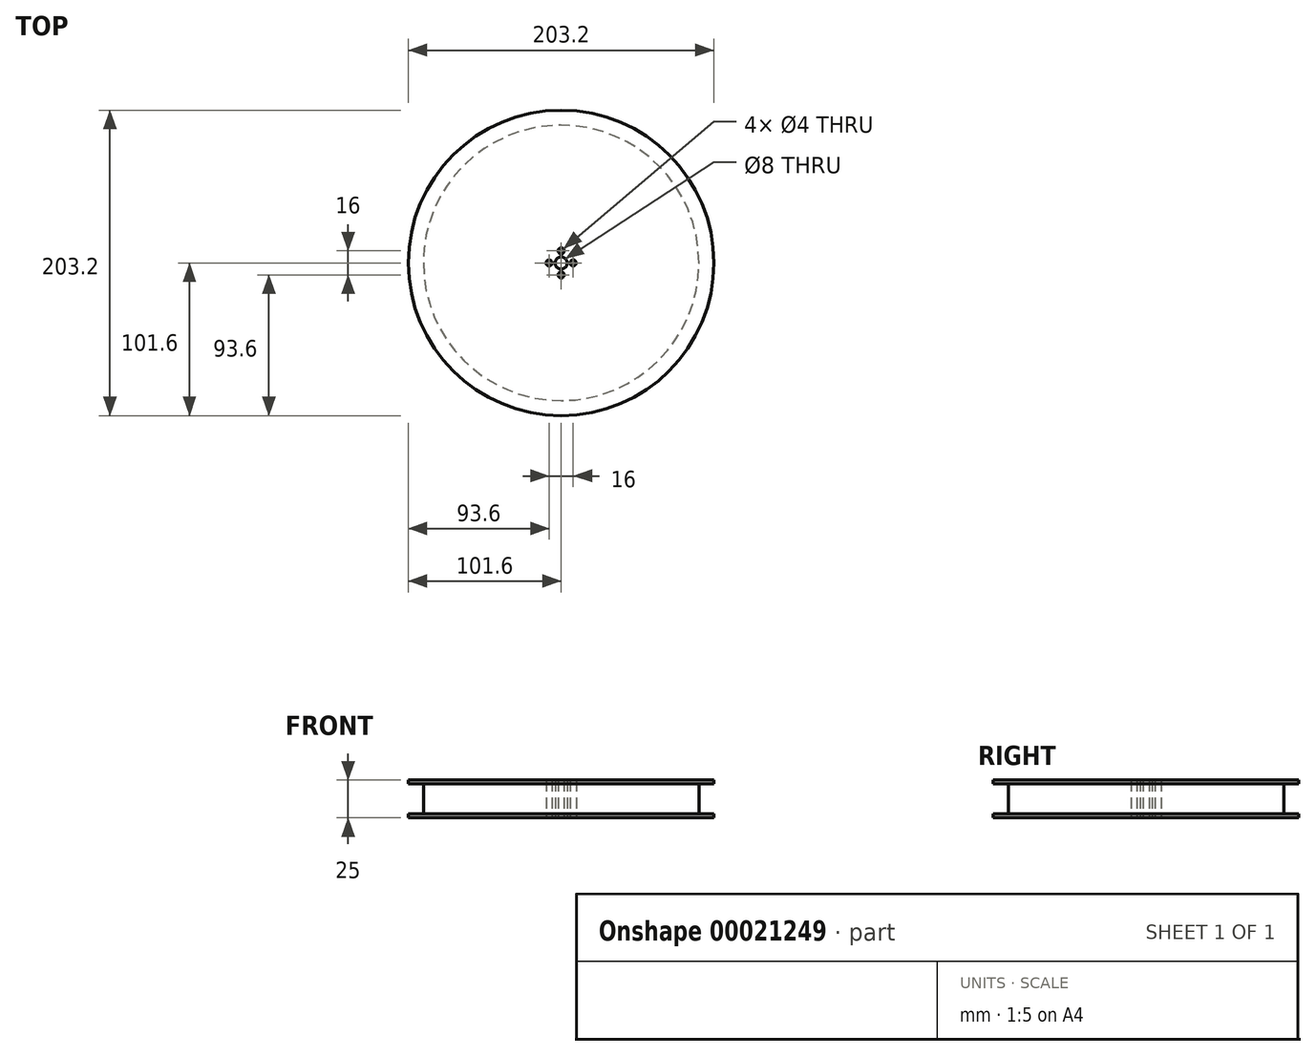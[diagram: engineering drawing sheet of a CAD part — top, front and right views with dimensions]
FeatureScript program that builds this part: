
annotation { "Feature Type Name" : "Feature", "Feature Type Description" : "" }
export const myFeature = defineFeature(function(context is Context, id is Id, definition is map)
    precondition{}
    {
        {
            var Q0;
            Q0=qCreatedBy(makeId("Top.planeOp"),FACE);
            var sketch = newSketch(context, id + "F0", { "sketchPlane" : qUnion([Q0])});
            skCircle(sketch, "E0", {"center": v(0, 0) * mm, "radius": 4 * mm});
            skCircle(sketch, "E1", {"center": v(8, 0) * mm, "radius": 2 * mm});
            skCircle(sketch, "E2.1.0", {"center": v(0, 8) * mm, "radius": 2 * mm});
            skCircle(sketch, "E2.2.0", {"center": v(-8, 0) * mm, "radius": 2 * mm});
            skCircle(sketch, "E2.3.0", {"center": v(0, -8) * mm, "radius": 2 * mm});
            skCircle(sketch, "E3", {"center": v(0, 0) * mm, "radius": 12 * mm});
            skCircle(sketch, "E4", {"center": v(0, 0) * mm, "radius": 101.6 * mm});
            skCircle(sketch, "E5", {"center": v(0, 0) * mm, "radius": 91.6 * mm});
            skSolve(sketch);
        }
        {
            var Q0;
            Q0=makeQuery(id+"F0.imprint","IMPRINT",FACE,{"disambiguationData":[TD([[makeQuery(id+"F0.imprint","IMPRINT",EDGE,{"derivedFrom":sQuery(id+"F0.wireOp",EDGE,"E0")}),-1.0]])]});
            var Q1;
            Q1=makeQuery(id+"F0.imprint","IMPRINT",FACE,{"disambiguationData":[TD([[makeQuery(id+"F0.imprint","IMPRINT",EDGE,{"derivedFrom":sQuery(id+"F0.wireOp",EDGE,"E3")}),-1.0]])]});
            extrude(context, id + "F1", {"entities" : qUnion([Q0, Q1]), "endBound" : BoundingType.SYMMETRIC, "depth" : 25 * mm});
        }
        {
            var Q0;
            Q0=makeQuery(id+"F0.imprint","IMPRINT",FACE,{"disambiguationData":[TD([[makeQuery(id+"F0.imprint","IMPRINT",EDGE,{"derivedFrom":sQuery(id+"F0.wireOp",EDGE,"E4")}),1.0]])]});
            extrude(context, id + "F2", {"entities" : qUnion([Q0]), "operationType" : NewBodyOperationType.ADD, "endBound" : BoundingType.SYMMETRIC, "depth" : 25 * mm});
        }
        {
            var Q0;
            Q0=makeQuery(id+"F0.imprint","IMPRINT",FACE,{"disambiguationData":[TD([[makeQuery(id+"F0.imprint","IMPRINT",EDGE,{"derivedFrom":sQuery(id+"F0.wireOp",EDGE,"E4")}),1.0]])]});
            extrude(context, id + "F3", {"entities" : qUnion([Q0]), "operationType" : NewBodyOperationType.REMOVE, "endBound" : BoundingType.SYMMETRIC, "oppositeDirection" : true, "depth" : 20 * mm});
        }
    });
